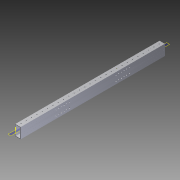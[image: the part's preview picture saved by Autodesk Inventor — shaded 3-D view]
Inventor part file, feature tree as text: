
AUTODESK INVENTOR PART (.ipt)
format: ipt  version: 2014 SP1 (Build 180222100, 222)  size: 952,832 bytes
history: native  units: in
note: dims shown in document units (in); Inventor stores cm internally (conversion verified against a paired STEP export)
features: reference x11, sketch x5, extrude x3, other x2, plane x1, mirror x1, imported_body x1
ambient origin geometry x8: Origin, YZ Plane, XZ Plane, XY Plane, X Axis, Y Axis, Z Axis, Center Point
bodies: Body1 (feature_tree)
feature tree (24):
  other  "Cut-Extrude2"
  other  "217-3453-STEP1"
  extrude  "Extrusion1"  Depth=15.9375in TaperAngle=0.0deg
  extrude  "Extrusion2"  [1 undecoded]
  extrude  "Extrusion3"  [1 undecoded]
  sketch  "Sketch4"
  sketch  "Sketch5"
  plane  "Work Plane1"
  mirror  "Mirror1"
  imported_body  "Base1"
  sketch  "Sketch1"  dims[d0=15.9375in d1=0.0in d2=15.9375in d3=0.0in]
  sketch  "Sketch2"  dims[d4=1.0in d5=0.0in d6=-1.0in]
  sketch  "Sketch3"
  reference  "Reference1"
  reference  "Reference2"
  reference  "Reference3"
  reference  "Reference4"
  reference  "Reference5"
  reference  "Reference6"
  reference  "Reference7"
  reference  "Reference8"
  reference  "Reference9"
  reference  "Reference10"
  reference  "Reference11"
note: 2 required parameter values undecoded (feature->parameter linkage not recoverable at this tier; creation-order binding heuristic only, values carry confidence <= 0.55)
